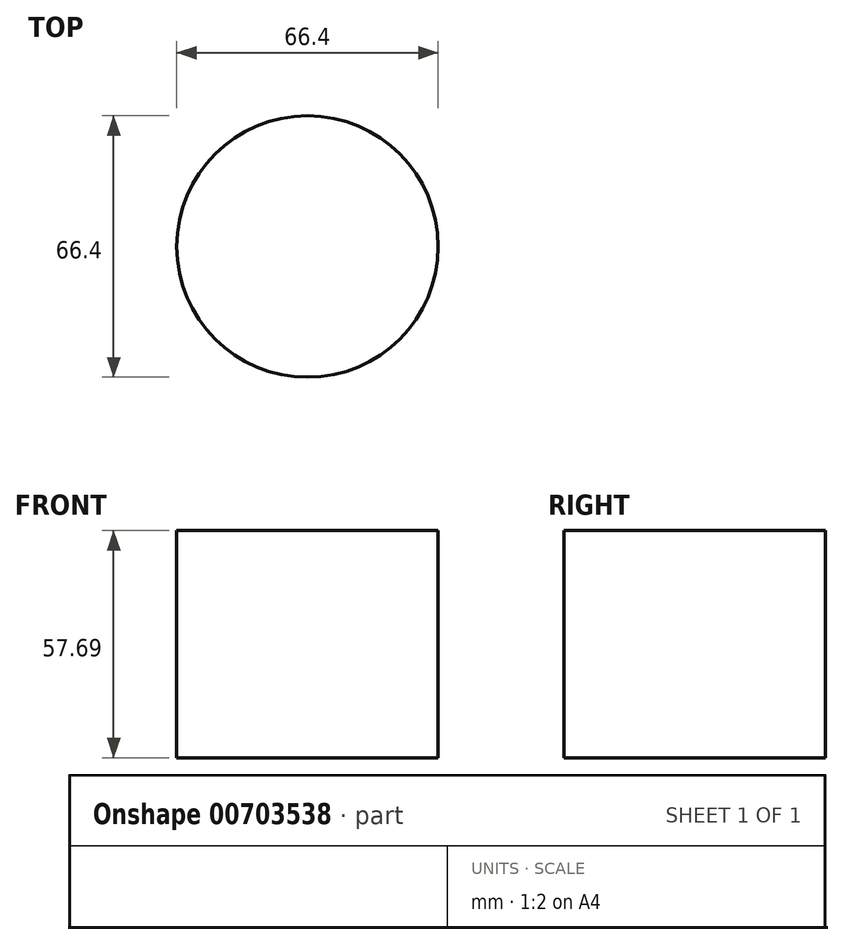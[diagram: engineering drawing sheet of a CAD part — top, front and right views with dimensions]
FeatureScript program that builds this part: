
annotation { "Feature Type Name" : "Feature", "Feature Type Description" : "" }
export const myFeature = defineFeature(function(context is Context, id is Id, definition is map)
    precondition{}
    {
        {
            var Q0;
            Q0=qCreatedBy(makeId("Front.planeOp"),FACE);
            var sketch = newSketch(context, id + "F0", { "sketchPlane" : qUnion([Q0])});
            skLineSegment(sketch, "E0.bottom", {"start": v(0, 33.88) * mm, "end": v(-32.52, 33.88) * mm});
            skLineSegment(sketch, "E0.top", {"start": v(0, 6.4) * mm, "end": v(-32.52, 6.4) * mm});
            skLineSegment(sketch, "E0.left", {"start": v(0, 33.88) * mm, "end": v(0, 6.4) * mm});
            skLineSegment(sketch, "E0.right", {"start": v(-32.52, 33.88) * mm, "end": v(-32.52, 6.4) * mm});
            skLineSegment(sketch, "E1.bottom", {"start": v(-67.08, 23.81) * mm, "end": v(-33.88, 23.81) * mm});
            skLineSegment(sketch, "E1.top", {"start": v(-67.08, -33.88) * mm, "end": v(-33.88, -33.88) * mm});
            skLineSegment(sketch, "E1.left", {"start": v(-67.08, 23.81) * mm, "end": v(-67.08, -33.88) * mm});
            skLineSegment(sketch, "E1.right", {"start": v(-33.88, 23.81) * mm, "end": v(-33.88, -33.88) * mm});
            skSolve(sketch);
        }
        {
            var Q0;
            Q0=makeQuery(id+"F0.imprint","IMPRINT",FACE,{"disambiguationData":[TD([[makeQuery(id+"F0.imprint","IMPRINT",EDGE,{"derivedFrom":sQuery(id+"F0.wireOp",EDGE,"E1.bottom")}),-1.0]])]});
            var Q1;
            Q1=sQuery(id+"F0.wireOp",EDGE,"E1.right");
            revolve(context, id + "F1", {"surfaceOperationType" : NewSurfaceOperationType.NEW, "entities" : qUnion([Q0]), "axis" : qUnion([Q1]), "revolveType" : RevolveType.FULL});
        }
    });
